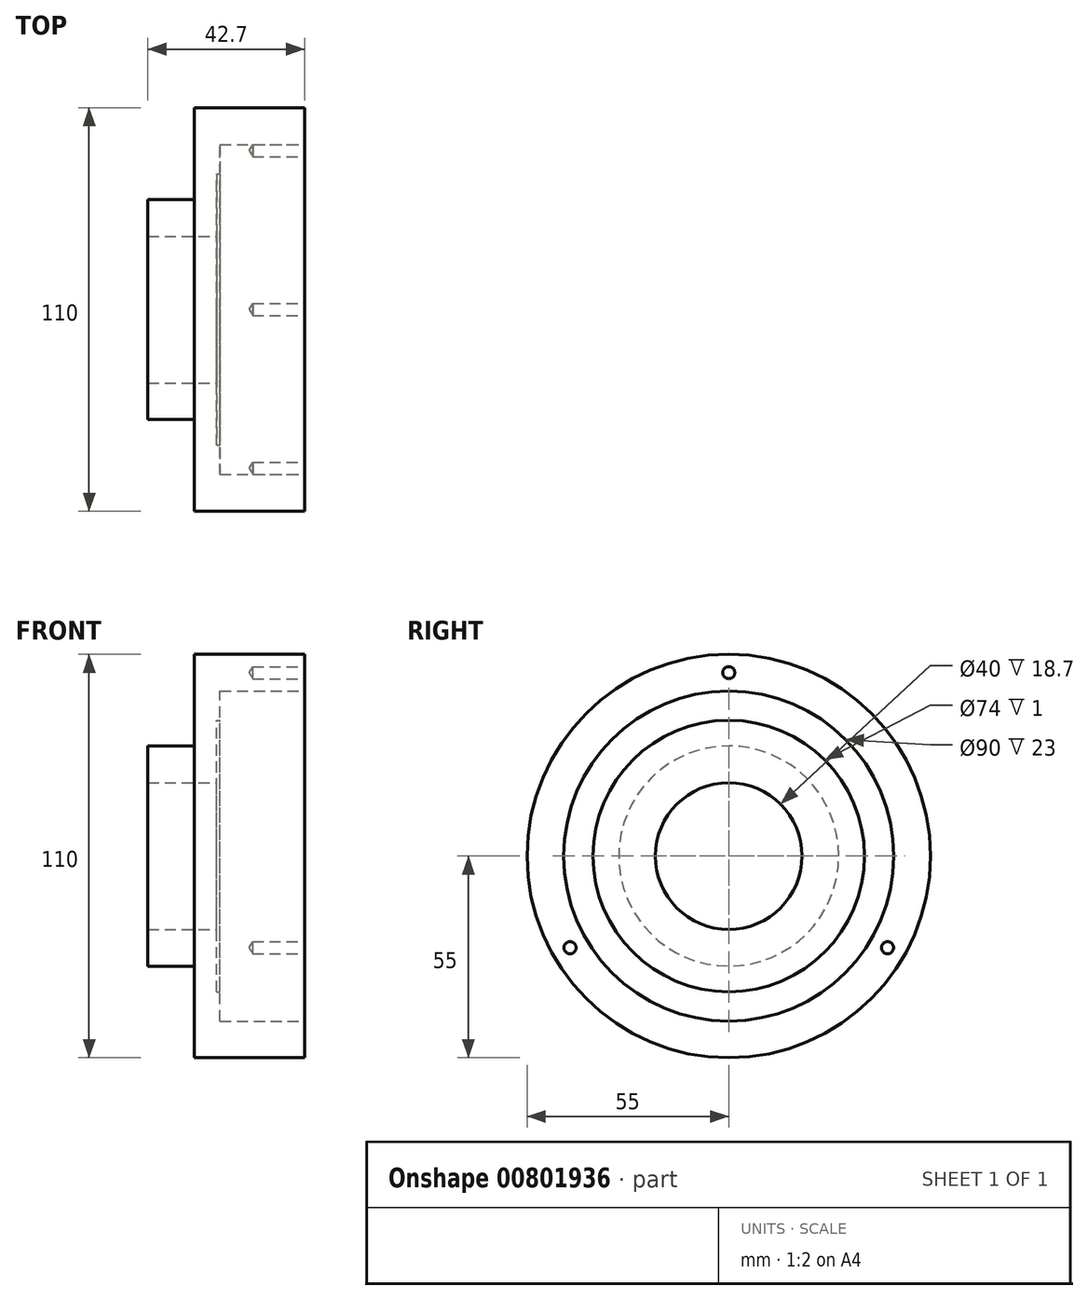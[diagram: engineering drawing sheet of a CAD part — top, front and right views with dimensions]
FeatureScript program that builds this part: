
annotation { "Feature Type Name" : "Feature", "Feature Type Description" : "" }
export const myFeature = defineFeature(function(context is Context, id is Id, definition is map)
    precondition{}
    {
        {
            var Q0;
            Q0=qCreatedBy(makeId("Front.planeOp"),FACE);
            var sketch = newSketch(context, id + "F0", { "sketchPlane" : qUnion([Q0])});
            skLineSegment(sketch, "E0", {"start": v(0, 30) * mm, "end": v(12.7, 30) * mm});
            skLineSegment(sketch, "E1", {"start": v(0, 30) * mm, "end": v(0, 20) * mm});
            skLineSegment(sketch, "E2", {"start": v(12.7, 30) * mm, "end": v(12.7, 55) * mm});
            skLineSegment(sketch, "E3", {"start": v(12.7, 55) * mm, "end": v(42.7, 55) * mm});
            skLineSegment(sketch, "E4", {"start": v(42.7, 55) * mm, "end": v(42.7, 45) * mm});
            skLineSegment(sketch, "E5", {"start": v(42.7, 45) * mm, "end": v(19.7, 45) * mm});
            skLineSegment(sketch, "E6", {"start": v(19.7, 45) * mm, "end": v(19.7, 37) * mm});
            skLineSegment(sketch, "E7", {"start": v(18.7, 0) * mm, "end": v(0, 0) * mm, "construction": true});
            skLineSegment(sketch, "E8", {"start": v(19.7, 37) * mm, "end": v(18.7, 37) * mm});
            skLineSegment(sketch, "E9", {"start": v(18.7, 37) * mm, "end": v(18.7, 20) * mm});
            skPoint(sketch, "E10.orphan", {"position": v(19.7, 0) * mm});
            skLineSegment(sketch, "E11", {"start": v(0, 20) * mm, "end": v(18.7, 20) * mm});
            skSolve(sketch);
        }
        {
            var Q0;
            Q0=qSketchRegion(id+"F0",true);
            var Q1;
            Q1=sQuery(id+"F0.wireOp",EDGE,"E7");
            revolve(context, id + "F1", {"surfaceOperationType" : NewSurfaceOperationType.NEW, "entities" : qUnion([Q0]), "axis" : qUnion([Q1]), "revolveType" : RevolveType.FULL});
        }
        {
            var Q0;
            Q0=makeQuery(id+"F1.opRevolve","SWEPT_FACE",FACE,{"disambiguationData":[OSD([sQuery(id+"F0.wireOp",EDGE,"E4")])]});
            var sketch = newSketch(context, id + "F2", { "sketchPlane" : qUnion([Q0])});
            skPoint(sketch, "E12", {"position": v(0, 50) * mm});
            skPoint(sketch, "E13.1.0", {"position": v(-43.3, -25) * mm});
            skPoint(sketch, "E13.2.0", {"position": v(43.3, -25) * mm});
            skPoint(sketch, "E13.center", {"position": v(0, 0) * mm});
            skSolve(sketch);
        }
        {
            var Q0;
            Q0=sQuery(id+"F2.wireOp",VERTEX,"E13.2.0");
            var Q1;
            Q1=sQuery(id+"F2.wireOp",VERTEX,"E13.1.0");
            var Q2;
            Q2=sQuery(id+"F2.wireOp",VERTEX,"E12");
            var Q3;
            Q3=makeQuery(id+"F1.opRevolve","SWEPT_BODY",BODY,{"disambiguationData":[OSD([sQuery(id+"F0.wireOp",EDGE,"E0"),sQuery(id+"F0.wireOp",EDGE,"E1"),sQuery(id+"F0.wireOp",EDGE,"E2"),sQuery(id+"F0.wireOp",EDGE,"E3"),sQuery(id+"F0.wireOp",EDGE,"E4"),sQuery(id+"F0.wireOp",EDGE,"E5"),sQuery(id+"F0.wireOp",EDGE,"E6"),sQuery(id+"F0.wireOp",EDGE,"E8"),sQuery(id+"F0.wireOp",EDGE,"E9"),sQuery(id+"F0.wireOp",EDGE,"E11")])]});
            hole(context, id + "F3", {"style" : HoleStyle.SIMPLE, "endStyle" : HoleEndStyle.BLIND, "standardTappedOrClearance" : lookupTablePath({ "standard" : "ISO", "engagement" : "75%", "pitch" : "0.7 mm", "size" : "M4", "type" : "Tapped" }), "standardBlindInLast" : lookupTablePath({ "standard" : "ISO", "fit" : "Normal", "engagement" : "75%", "pitch" : "0.7 mm", "size" : "M4", "type" : "Clearance & tapped" }), "holeDiameter" : 3.3 * mm, "majorDiameter" : 4 * mm, "showTappedDepth" : true, "holeDepth" : 14.1 * mm, "tappedDepth" : 12 * mm, "tapClearance" : 3, "startFromSketch" : true, "locations" : qUnion([Q0, Q1, Q2]), "scope" : qUnion([Q3])});
        }
    });
